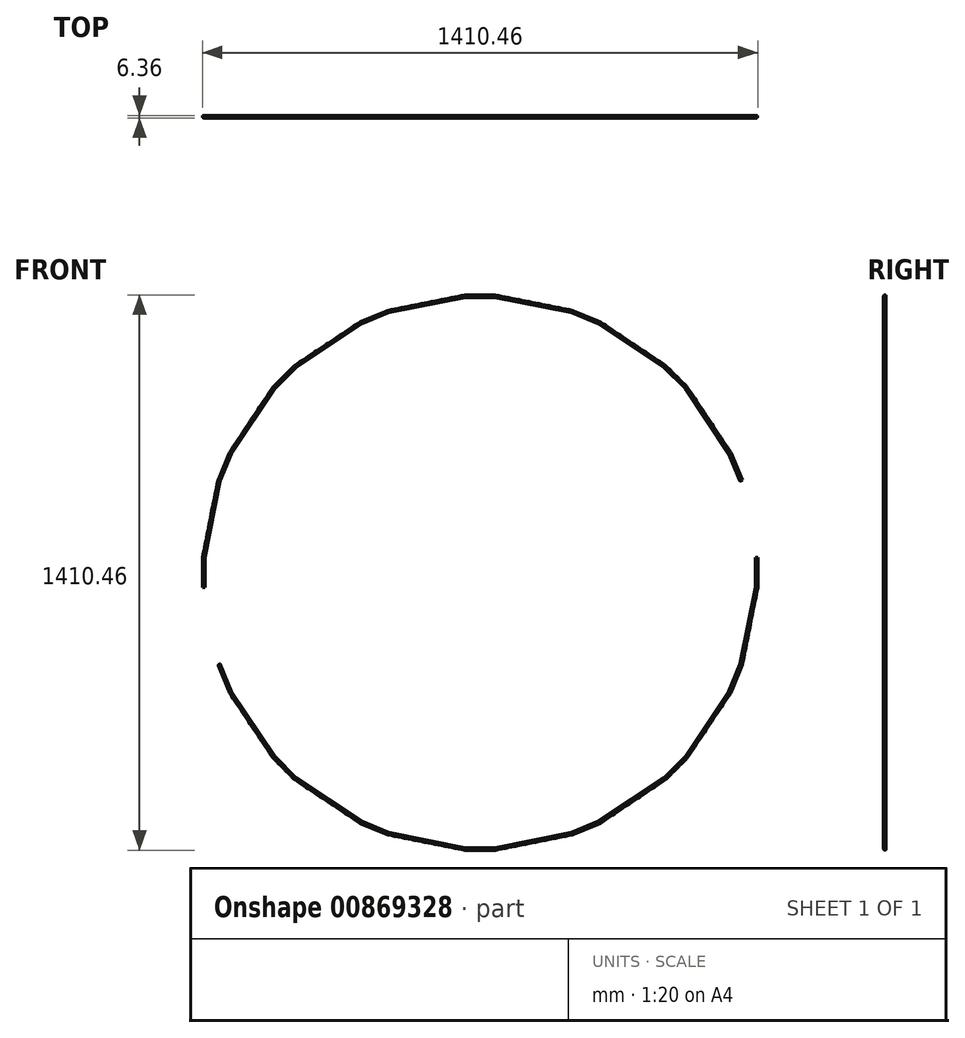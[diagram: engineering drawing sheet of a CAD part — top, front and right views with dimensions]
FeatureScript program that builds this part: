
annotation { "Feature Type Name" : "Feature", "Feature Type Description" : "" }
export const myFeature = defineFeature(function(context is Context, id is Id, definition is map)
    precondition{}
    {
        {
            var Q0;
            Q0=qCreatedBy(makeId("Front.planeOp"),FACE);
            var sketch = newSketch(context, id + "F0", { "sketchPlane" : qUnion([Q0])});
            skLineSegment(sketch, "E0", {"start": v(-698.88, 38.1) * mm, "end": v(-698.88, -38.1) * mm});
            skLineSegment(sketch, "E1", {"start": v(698.88, 38.1) * mm, "end": v(698.88, -38.1) * mm});
            skLineSegment(sketch, "E2", {"start": v(-38.1, 698.88) * mm, "end": v(38.1, 698.88) * mm});
            skLineSegment(sketch, "E3", {"start": v(-38.1, -698.88) * mm, "end": v(38.1, -698.88) * mm});
            skLineSegment(sketch, "E4", {"start": v(521.12, -467.24) * mm, "end": v(467.24, -521.12) * mm});
            skLineSegment(sketch, "E5", {"start": v(-521.12, -467.24) * mm, "end": v(-467.24, -521.12) * mm});
            skLineSegment(sketch, "E6", {"start": v(467.24, 521.12) * mm, "end": v(521.12, 467.24) * mm});
            skLineSegment(sketch, "E7", {"start": v(-467.24, 521.12) * mm, "end": v(-521.12, 467.24) * mm});
            skLineSegment(sketch, "E8", {"start": v(232.25, -660.26) * mm, "end": v(302.65, -631.1) * mm});
            skLineSegment(sketch, "E9", {"start": v(660.26, -232.25) * mm, "end": v(631.1, -302.65) * mm});
            skLineSegment(sketch, "E10", {"start": v(302.65, -631.1) * mm, "end": v(467.24, -521.12) * mm});
            skLineSegment(sketch, "E11", {"start": v(521.12, -467.24) * mm, "end": v(631.1, -302.65) * mm});
            skLineSegment(sketch, "E12", {"start": v(660.26, -232.25) * mm, "end": v(698.88, -38.1) * mm});
            skLineSegment(sketch, "E13", {"start": v(232.25, -660.26) * mm, "end": v(38.1, -698.88) * mm});
            skLineSegment(sketch, "E14", {"start": v(631.1, 302.65) * mm, "end": v(660.26, 232.25) * mm});
            skLineSegment(sketch, "E15", {"start": v(232.25, 660.26) * mm, "end": v(302.65, 631.1) * mm});
            skLineSegment(sketch, "E16", {"start": v(-302.65, 631.1) * mm, "end": v(-232.25, 660.26) * mm});
            skLineSegment(sketch, "E17", {"start": v(-660.26, 232.25) * mm, "end": v(-631.1, 302.65) * mm});
            skLineSegment(sketch, "E18", {"start": v(-660.26, -232.25) * mm, "end": v(-631.1, -302.65) * mm});
            skLineSegment(sketch, "E19", {"start": v(-302.65, -631.1) * mm, "end": v(-232.25, -660.26) * mm});
            skLineSegment(sketch, "E20", {"start": v(-38.1, -698.88) * mm, "end": v(-232.25, -660.26) * mm});
            skLineSegment(sketch, "E21", {"start": v(-302.65, -631.1) * mm, "end": v(-467.24, -521.12) * mm});
            skLineSegment(sketch, "E22", {"start": v(-521.12, -467.24) * mm, "end": v(-631.1, -302.65) * mm});
            skLineSegment(sketch, "E23", {"start": v(-698.88, 38.1) * mm, "end": v(-660.26, 232.25) * mm});
            skLineSegment(sketch, "E24", {"start": v(-631.1, 302.65) * mm, "end": v(-521.12, 467.24) * mm});
            skLineSegment(sketch, "E25", {"start": v(-467.24, 521.12) * mm, "end": v(-302.65, 631.1) * mm});
            skLineSegment(sketch, "E26", {"start": v(38.1, 698.88) * mm, "end": v(232.25, 660.26) * mm});
            skLineSegment(sketch, "E27", {"start": v(302.65, 631.1) * mm, "end": v(467.24, 521.12) * mm});
            skLineSegment(sketch, "E28", {"start": v(521.12, 467.24) * mm, "end": v(631.1, 302.65) * mm});
            skLineSegment(sketch, "E29", {"start": v(-232.25, 660.26) * mm, "end": v(-38.1, 698.88) * mm});
            skSolve(sketch);
        }
        {
            var Q0;
            Q0=qCreatedBy(makeId("Right.planeOp"),FACE);
            var sketch = newSketch(context, id + "F1", { "sketchPlane" : qUnion([Q0])});
            skCircle(sketch, "E30", {"center": v(0, 702.06) * mm, "radius": 3.17 * mm});
            skSolve(sketch);
        }
        {
            var Q0;
            Q0=qCreatedBy(makeId("Top.planeOp"),FACE);
            var sketch = newSketch(context, id + "F2", { "sketchPlane" : qUnion([Q0])});
            skCircle(sketch, "E31", {"center": v(702.06, 0) * mm, "radius": 3.18 * mm});
            skSolve(sketch);
        }
        {
            var Q0;
            Q0=makeQuery(id+"F1.imprint","IMPRINT",FACE,{"disambiguationData":[TD([[makeQuery(id+"F1.imprint","IMPRINT",EDGE,{"derivedFrom":sQuery(id+"F1.wireOp",EDGE,"E30")}),1.0]])]});
            var Q1;
            Q1=sQuery(id+"F0.wireOp",EDGE,"E0");
            var Q2;
            Q2=sQuery(id+"F0.wireOp",EDGE,"E23");
            var Q3;
            Q3=sQuery(id+"F0.wireOp",EDGE,"E17");
            var Q4;
            Q4=sQuery(id+"F0.wireOp",EDGE,"E24");
            var Q5;
            Q5=sQuery(id+"F0.wireOp",EDGE,"E7");
            var Q6;
            Q6=sQuery(id+"F0.wireOp",EDGE,"E25");
            var Q7;
            Q7=sQuery(id+"F0.wireOp",EDGE,"E29");
            var Q8;
            Q8=sQuery(id+"F0.wireOp",EDGE,"E16");
            var Q9;
            Q9=sQuery(id+"F0.wireOp",EDGE,"E2");
            var Q10;
            Q10=sQuery(id+"F0.wireOp",EDGE,"E26");
            var Q11;
            Q11=sQuery(id+"F0.wireOp",EDGE,"E15");
            var Q12;
            Q12=sQuery(id+"F0.wireOp",EDGE,"E27");
            var Q13;
            Q13=sQuery(id+"F0.wireOp",EDGE,"E14");
            var Q14;
            Q14=sQuery(id+"F0.wireOp",EDGE,"E28");
            var Q15;
            Q15=sQuery(id+"F0.wireOp",EDGE,"E6");
            sweep(context, id + "F3", {"profiles" : qUnion([Q0]), "path" : qUnion([Q1, Q2, Q3, Q4, Q5, Q6, Q7, Q8, Q9, Q10, Q11, Q12, Q13, Q14, Q15])});
        }
        {
            var Q0;
            Q0=makeQuery(id+"F2.imprint","IMPRINT",FACE,{"disambiguationData":[TD([[makeQuery(id+"F2.imprint","IMPRINT",EDGE,{"derivedFrom":sQuery(id+"F2.wireOp",EDGE,"E31")}),1.0]])]});
            var Q1;
            Q1=sQuery(id+"F0.wireOp",EDGE,"E20");
            var Q2;
            Q2=sQuery(id+"F0.wireOp",EDGE,"E21");
            var Q3;
            Q3=sQuery(id+"F0.wireOp",EDGE,"E22");
            var Q4;
            Q4=sQuery(id+"F0.wireOp",EDGE,"E11");
            var Q5;
            Q5=sQuery(id+"F0.wireOp",EDGE,"E10");
            var Q6;
            Q6=sQuery(id+"F0.wireOp",EDGE,"E1");
            var Q7;
            Q7=sQuery(id+"F0.wireOp",EDGE,"E5");
            var Q8;
            Q8=sQuery(id+"F0.wireOp",EDGE,"E3");
            var Q9;
            Q9=sQuery(id+"F0.wireOp",EDGE,"E18");
            var Q10;
            Q10=sQuery(id+"F0.wireOp",EDGE,"E8");
            var Q11;
            Q11=sQuery(id+"F0.wireOp",EDGE,"E19");
            var Q12;
            Q12=sQuery(id+"F0.wireOp",EDGE,"E13");
            var Q13;
            Q13=sQuery(id+"F0.wireOp",EDGE,"E4");
            var Q14;
            Q14=sQuery(id+"F0.wireOp",EDGE,"E9");
            var Q15;
            Q15=sQuery(id+"F0.wireOp",EDGE,"E12");
            sweep(context, id + "F4", {"profiles" : qUnion([Q0]), "path" : qUnion([Q1, Q2, Q3, Q4, Q5, Q6, Q7, Q8, Q9, Q10, Q11, Q12, Q13, Q14, Q15])});
        }
    });
